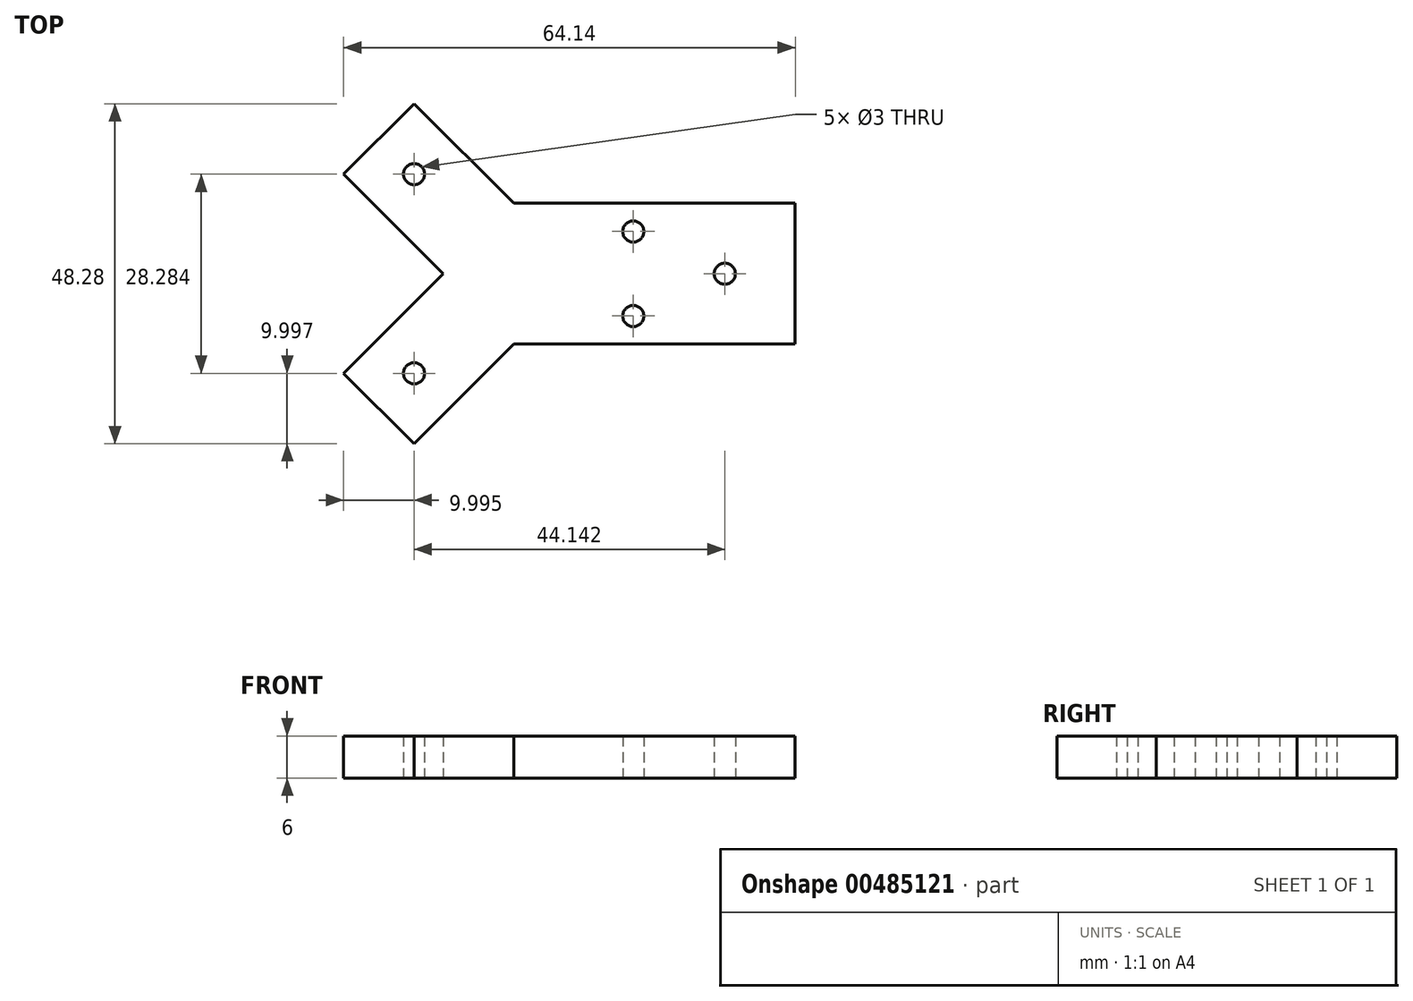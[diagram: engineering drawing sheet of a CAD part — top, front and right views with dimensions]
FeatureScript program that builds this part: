
annotation { "Feature Type Name" : "Feature", "Feature Type Description" : "" }
export const myFeature = defineFeature(function(context is Context, id is Id, definition is map)
    precondition{}
    {
        {
            var Q0;
            Q0=qCreatedBy(makeId("Top.planeOp"),FACE);
            var sketch = newSketch(context, id + "F0", { "sketchPlane" : qUnion([Q0])});
            skLineSegment(sketch, "E0.bottom", {"start": v(-20.1, 11.33) * mm, "end": v(19.9, 11.33) * mm, "construction": true});
            skLineSegment(sketch, "E0.top", {"start": v(-20.1, -8.67) * mm, "end": v(19.9, -8.67) * mm, "construction": true});
            skLineSegment(sketch, "E0.left", {"start": v(-20.1, 11.33) * mm, "end": v(-20.1, -8.67) * mm, "construction": true});
            skLineSegment(sketch, "E0.right", {"start": v(19.9, 11.33) * mm, "end": v(19.9, -8.67) * mm, "construction": true});
            skLineSegment(sketch, "E1", {"start": v(-20.1, 7.33) * mm, "end": v(19.9, 7.33) * mm, "construction": true});
            skLineSegment(sketch, "E2", {"start": v(-20.1, -4.67) * mm, "end": v(19.9, -4.67) * mm, "construction": true});
            skLineSegment(sketch, "E3", {"start": v(19.9, 1.33) * mm, "end": v(-50.09, 1.33) * mm, "construction": true});
            skPoint(sketch, "E3.endSnap0", {"position": v(-20.1, 1.33) * mm});
            skPoint(sketch, "E4", {"position": v(-30.1, 1.33) * mm});
            skLineSegment(sketch, "E5", {"start": v(-20.1, 11.33) * mm, "end": v(-30.1, 1.33) * mm, "construction": true});
            skLineSegment(sketch, "E6", {"start": v(-20.1, -8.67) * mm, "end": v(-30.1, 1.33) * mm, "construction": true});
            skLineSegment(sketch, "E7", {"start": v(-30.1, 1.33) * mm, "end": v(-55.97, 27.21) * mm, "construction": true});
            skLineSegment(sketch, "E8", {"start": v(-20.1, 11.33) * mm, "end": v(-42.97, 34.2) * mm, "construction": true});
            skLineSegment(sketch, "E9", {"start": v(-20.1, -8.67) * mm, "end": v(-39.9, -28.49) * mm, "construction": true});
            skLineSegment(sketch, "E10", {"start": v(-30.1, 1.33) * mm, "end": v(-54.5, -23.08) * mm, "construction": true});
            skLineSegment(sketch, "E11", {"start": v(-34.23, -22.81) * mm, "end": v(-44.23, -12.81) * mm, "construction": true});
            skLineSegment(sketch, "E12", {"start": v(-34.23, 25.47) * mm, "end": v(-44.23, 15.47) * mm, "construction": true});
            skLineSegment(sketch, "E13", {"start": v(-34.23, 5.47) * mm, "end": v(-24.23, 15.47) * mm, "construction": true});
            skLineSegment(sketch, "E14", {"start": v(-34.23, -2.81) * mm, "end": v(-24.23, -12.81) * mm, "construction": true});
            skLineSegment(sketch, "E15", {"start": v(-34.23, 25.47) * mm, "end": v(-34.23, 5.47) * mm, "construction": true});
            skLineSegment(sketch, "E16", {"start": v(-44.23, 15.47) * mm, "end": v(-24.23, 15.47) * mm, "construction": true});
            skLineSegment(sketch, "E17", {"start": v(-34.23, -2.81) * mm, "end": v(-34.23, -22.81) * mm, "construction": true});
            skLineSegment(sketch, "E18", {"start": v(-24.23, -12.81) * mm, "end": v(-44.23, -12.81) * mm, "construction": true});
            skCircle(sketch, "E19", {"center": v(-34.23, 15.47) * mm, "radius": 1.5 * mm});
            skCircle(sketch, "E20", {"center": v(-34.23, -12.81) * mm, "radius": 1.5 * mm});
            skLineSegment(sketch, "E21", {"start": v(9.9, 11.33) * mm, "end": v(9.9, -8.67) * mm, "construction": true});
            skLineSegment(sketch, "E22", {"start": v(-3.1, 11.33) * mm, "end": v(-3.1, -8.67) * mm, "construction": true});
            skLineSegment(sketch, "E23", {"start": v(-34.23, 25.47) * mm, "end": v(-20.1, 11.33) * mm});
            skLineSegment(sketch, "E24", {"start": v(-20.1, 11.33) * mm, "end": v(19.9, 11.33) * mm});
            skLineSegment(sketch, "E25", {"start": v(19.9, 11.33) * mm, "end": v(19.9, -8.67) * mm});
            skLineSegment(sketch, "E26", {"start": v(19.9, -8.67) * mm, "end": v(-20.1, -8.67) * mm});
            skLineSegment(sketch, "E27", {"start": v(-20.1, -8.67) * mm, "end": v(-34.23, -22.81) * mm});
            skLineSegment(sketch, "E28", {"start": v(-34.23, -22.81) * mm, "end": v(-44.23, -12.81) * mm});
            skLineSegment(sketch, "E29", {"start": v(-44.23, -12.81) * mm, "end": v(-30.1, 1.33) * mm});
            skLineSegment(sketch, "E30", {"start": v(-30.1, 1.33) * mm, "end": v(-44.23, 15.47) * mm});
            skLineSegment(sketch, "E31", {"start": v(-44.23, 15.47) * mm, "end": v(-34.23, 25.47) * mm});
            skCircle(sketch, "E32", {"center": v(-3.1, 7.33) * mm, "radius": 1.5 * mm});
            skCircle(sketch, "E33", {"center": v(-3.1, -4.67) * mm, "radius": 1.5 * mm});
            skCircle(sketch, "E34", {"center": v(9.9, 1.33) * mm, "radius": 1.5 * mm});
            skSolve(sketch);
        }
        {
            var Q0;
            Q0=makeQuery(id+"F0.imprint","IMPRINT",FACE,{"disambiguationData":[TD([[makeQuery(id+"F0.imprint","IMPRINT",EDGE,{"derivedFrom":sQuery(id+"F0.wireOp",EDGE,"E19")}),-1.0]])]});
            extrude(context, id + "F1", {"entities" : qUnion([Q0]), "depth" : 6 * mm, "offsetDistance" : 25 * mm});
        }
    });
